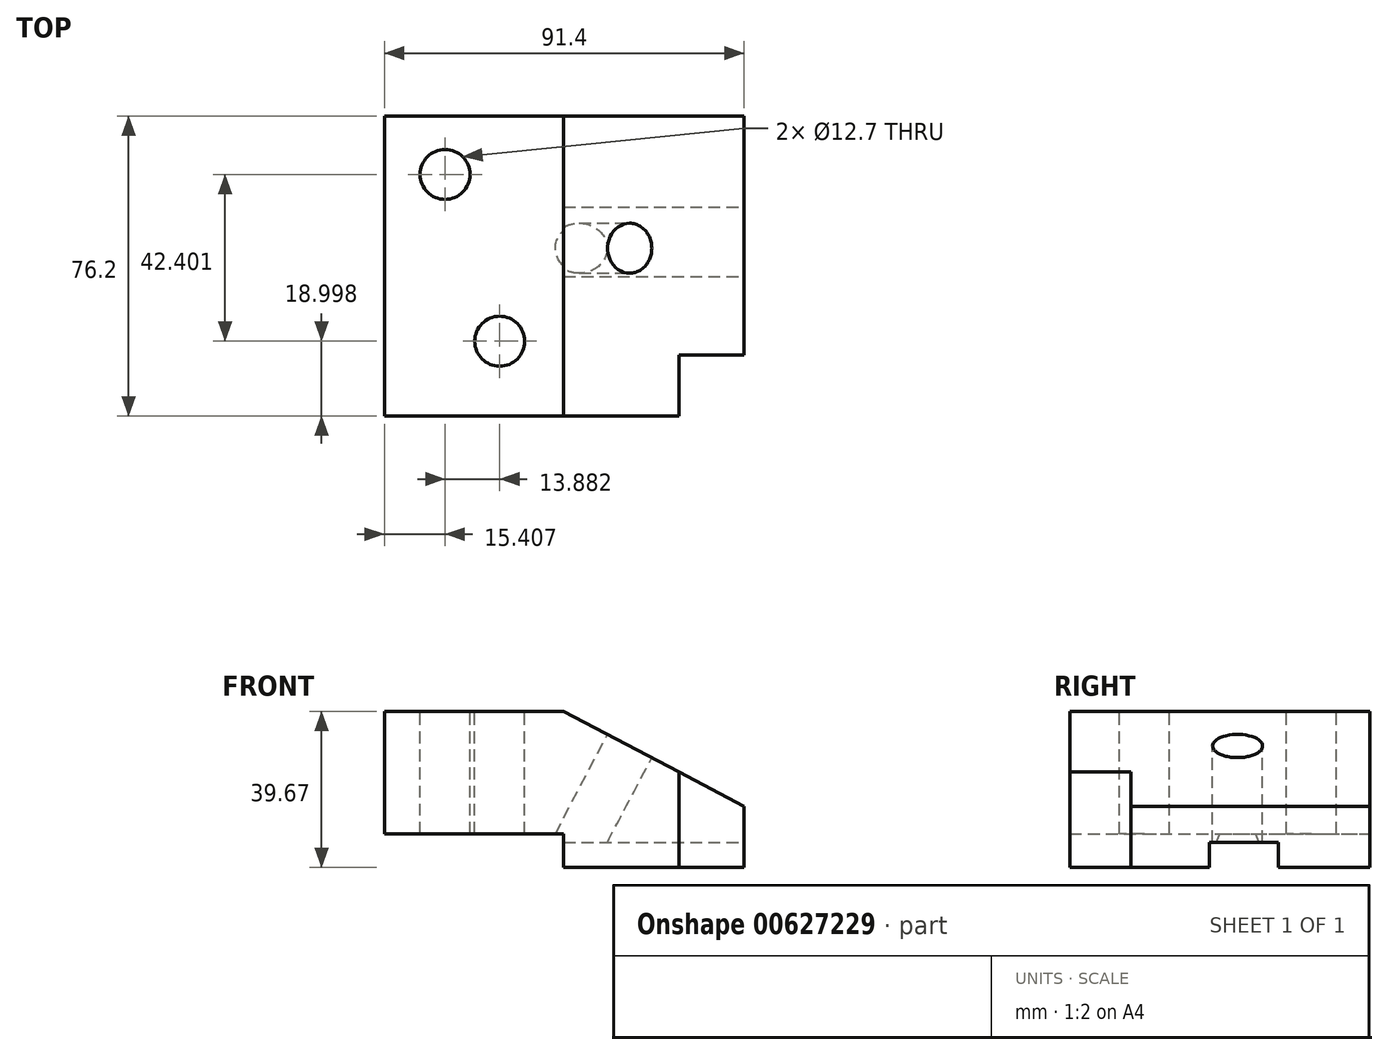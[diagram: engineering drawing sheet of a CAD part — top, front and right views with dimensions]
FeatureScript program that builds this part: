
annotation { "Feature Type Name" : "Feature", "Feature Type Description" : "" }
export const myFeature = defineFeature(function(context is Context, id is Id, definition is map)
    precondition{}
    {
        {
            var Q0;
            Q0=qCreatedBy(makeId("Front.planeOp"),FACE);
            var sketch = newSketch(context, id + "F0", { "sketchPlane" : qUnion([Q0])});
            skLineSegment(sketch, "E0", {"start": v(-57.79, 17.42) * mm, "end": v(-12.28, 17.42) * mm});
            skLineSegment(sketch, "E1", {"start": v(-12.28, 17.42) * mm, "end": v(33.6, -6.7) * mm});
            skLineSegment(sketch, "E2", {"start": v(33.6, -6.7) * mm, "end": v(33.6, -22.25) * mm});
            skLineSegment(sketch, "E3", {"start": v(33.6, -22.25) * mm, "end": v(-12.28, -22.25) * mm});
            skLineSegment(sketch, "E4", {"start": v(-12.28, -22.25) * mm, "end": v(-12.28, -13.7) * mm});
            skLineSegment(sketch, "E5", {"start": v(-12.28, -13.7) * mm, "end": v(-57.79, -13.7) * mm});
            skLineSegment(sketch, "E6", {"start": v(-57.79, 17.42) * mm, "end": v(-57.79, -13.7) * mm});
            skLineSegment(sketch, "E7", {"start": v(14.55, -22.25) * mm, "end": v(14.55, 3.32) * mm});
            skSolve(sketch);
        }
        {
            var Q0;
            {var subQ2=sQuery(id+"F0.wireOp",EDGE,"E0");Q0=makeQuery(id+"F0.imprint","IMPRINT",FACE,{"disambiguationData":[TD([[makeQuery(id+"F0.imprint","IMPRINT",EDGE,{"derivedFrom":subQ2}),-1.0]])]});}
            var Q1;
            {var subQ0=sQuery(id+"F0.wireOp",EDGE,"E2");Q1=makeQuery(id+"F0.imprint","IMPRINT",FACE,{"disambiguationData":[TD([[makeQuery(id+"F0.imprint","IMPRINT",EDGE,{"derivedFrom":subQ0}),-1.0]])]});}
            extrude(context, id + "F1", {"entities" : qUnion([Q0, Q1]), "depth" : 76.2 * mm, "offsetDistance" : 25.4 * mm});
        }
        {
            var Q0;
            Q0=makeQuery(id+"F1.opExtrude","SWEPT_FACE",FACE,{"disambiguationData":[OSD([sQuery(id+"F0.wireOp",EDGE,"E0")])]});
            var sketch = newSketch(context, id + "F2", { "sketchPlane" : qUnion([Q0])});
            skPoint(sketch, "E8", {"position": v(-42.38, -14.8) * mm});
            skPoint(sketch, "E9", {"position": v(-28.5, -57.2) * mm});
            skSolve(sketch);
        }
        {
            var Q0;
            Q0=sQuery(id+"F2.wireOp",VERTEX,"E8");
            var Q1;
            Q1=sQuery(id+"F2.wireOp",VERTEX,"E9");
            var Q2;
            Q2=makeQuery(id+"F1.opExtrude","SWEPT_BODY",BODY,{"disambiguationData":[OSD([sQuery(id+"F0.wireOp",EDGE,"E0"),sQuery(id+"F0.wireOp",EDGE,"E1"),sQuery(id+"F0.wireOp",EDGE,"E2"),sQuery(id+"F0.wireOp",EDGE,"E3"),sQuery(id+"F0.wireOp",EDGE,"E4"),sQuery(id+"F0.wireOp",EDGE,"E5"),sQuery(id+"F0.wireOp",EDGE,"E6")])]});
            hole(context, id + "F3", {"style" : HoleStyle.SIMPLE, "endStyle" : HoleEndStyle.THROUGH, "holeDiameter" : 12.7 * mm, "majorDiameter" : 6.35 * mm, "isTappedThrough" : true, "tappedDepth" : 12.7 * mm, "tapClearance" : 3, "locations" : qUnion([Q0, Q1]), "scope" : qUnion([Q2])});
        }
        {
            var Q0;
            Q0=makeQuery(id+"F1.opExtrude","CAP_FACE",FACE,{"disambiguationData":[OSD([sQuery(id+"F0.wireOp",EDGE,"E0"),sQuery(id+"F0.wireOp",EDGE,"E1"),sQuery(id+"F0.wireOp",EDGE,"E2"),sQuery(id+"F0.wireOp",EDGE,"E3"),sQuery(id+"F0.wireOp",EDGE,"E4"),sQuery(id+"F0.wireOp",EDGE,"E5"),sQuery(id+"F0.wireOp",EDGE,"E6")])],"isStart":false});
            var sketch = newSketch(context, id + "F4", { "sketchPlane" : qUnion([Q0])});
            skLineSegment(sketch, "E10", {"start": v(17.01, 2.02) * mm, "end": v(17.01, -22.25) * mm});
            skLineSegment(sketch, "E11", {"start": v(17.01, -22.25) * mm, "end": v(33.6, -22.25) * mm});
            skLineSegment(sketch, "E12", {"start": v(33.6, -22.25) * mm, "end": v(33.6, -6.7) * mm});
            skSolve(sketch);
        }
        {
            var Q0;
            {var subQ0=sQuery(id+"F4.wireOp",EDGE,"E10");Q0=makeQuery(id+"F4.imprint","IMPRINT",FACE,{"disambiguationData":[TD([[makeQuery(id+"F4.imprint","IMPRINT",EDGE,{"derivedFrom":subQ0}),1.0]])]});}
            extrude(context, id + "F5", {"entities" : qUnion([Q0]), "operationType" : NewBodyOperationType.REMOVE, "oppositeDirection" : true, "depth" : 15.5 * mm, "offsetDistance" : 25.4 * mm});
        }
        {
            var Q0;
            Q0=makeQuery(id+"F1.opExtrude","SWEPT_FACE",FACE,{"disambiguationData":[OSD([sQuery(id+"F0.wireOp",EDGE,"E2")])]});
            var sketch = newSketch(context, id + "F6", { "sketchPlane" : qUnion([Q0])});
            skLineSegment(sketch, "E13.bottom", {"start": v(-40.7, -22.25) * mm, "end": v(-23.15, -22.25) * mm});
            skLineSegment(sketch, "E13.top", {"start": v(-40.7, -15.89) * mm, "end": v(-23.15, -15.89) * mm});
            skLineSegment(sketch, "E13.left", {"start": v(-40.7, -22.25) * mm, "end": v(-40.7, -15.89) * mm});
            skLineSegment(sketch, "E13.right", {"start": v(-23.15, -22.25) * mm, "end": v(-23.15, -15.89) * mm});
            skSolve(sketch);
        }
        {
            var Q0;
            Q0=makeQuery(id+"F6.imprint","IMPRINT",FACE,{"disambiguationData":[TD([[makeQuery(id+"F6.imprint","IMPRINT",EDGE,{"derivedFrom":sQuery(id+"F6.wireOp",EDGE,"E13.bottom")}),1.0]])]});
            extrude(context, id + "F7", {"entities" : qUnion([Q0]), "operationType" : NewBodyOperationType.REMOVE, "oppositeDirection" : true, "depth" : 76.2 * mm, "offsetDistance" : 25.4 * mm});
        }
        {
            var Q0;
            Q0=makeQuery(id+"F1.opExtrude","SWEPT_FACE",FACE,{"disambiguationData":[OSD([sQuery(id+"F0.wireOp",EDGE,"E1")])]});
            var sketch = newSketch(context, id + "F8", { "sketchPlane" : qUnion([Q0])});
            skPoint(sketch, "E14", {"position": v(0, -33.57) * mm});
            skSolve(sketch);
        }
        {
            var Q0;
            Q0=sQuery(id+"F8.wireOp",VERTEX,"E14");
            var Q1;
            Q1=makeQuery(id+"F1.opExtrude","SWEPT_BODY",BODY,{"disambiguationData":[OSD([sQuery(id+"F0.wireOp",EDGE,"E0"),sQuery(id+"F0.wireOp",EDGE,"E1"),sQuery(id+"F0.wireOp",EDGE,"E2"),sQuery(id+"F0.wireOp",EDGE,"E3"),sQuery(id+"F0.wireOp",EDGE,"E4"),sQuery(id+"F0.wireOp",EDGE,"E5"),sQuery(id+"F0.wireOp",EDGE,"E6")])]});
            hole(context, id + "F9", {"style" : HoleStyle.SIMPLE, "endStyle" : HoleEndStyle.THROUGH, "holeDiameter" : 12.7 * mm, "majorDiameter" : 6.35 * mm, "isTappedThrough" : true, "tappedDepth" : 12.7 * mm, "tapClearance" : 3, "locations" : qUnion([Q0]), "scope" : qUnion([Q1])});
        }
    });
